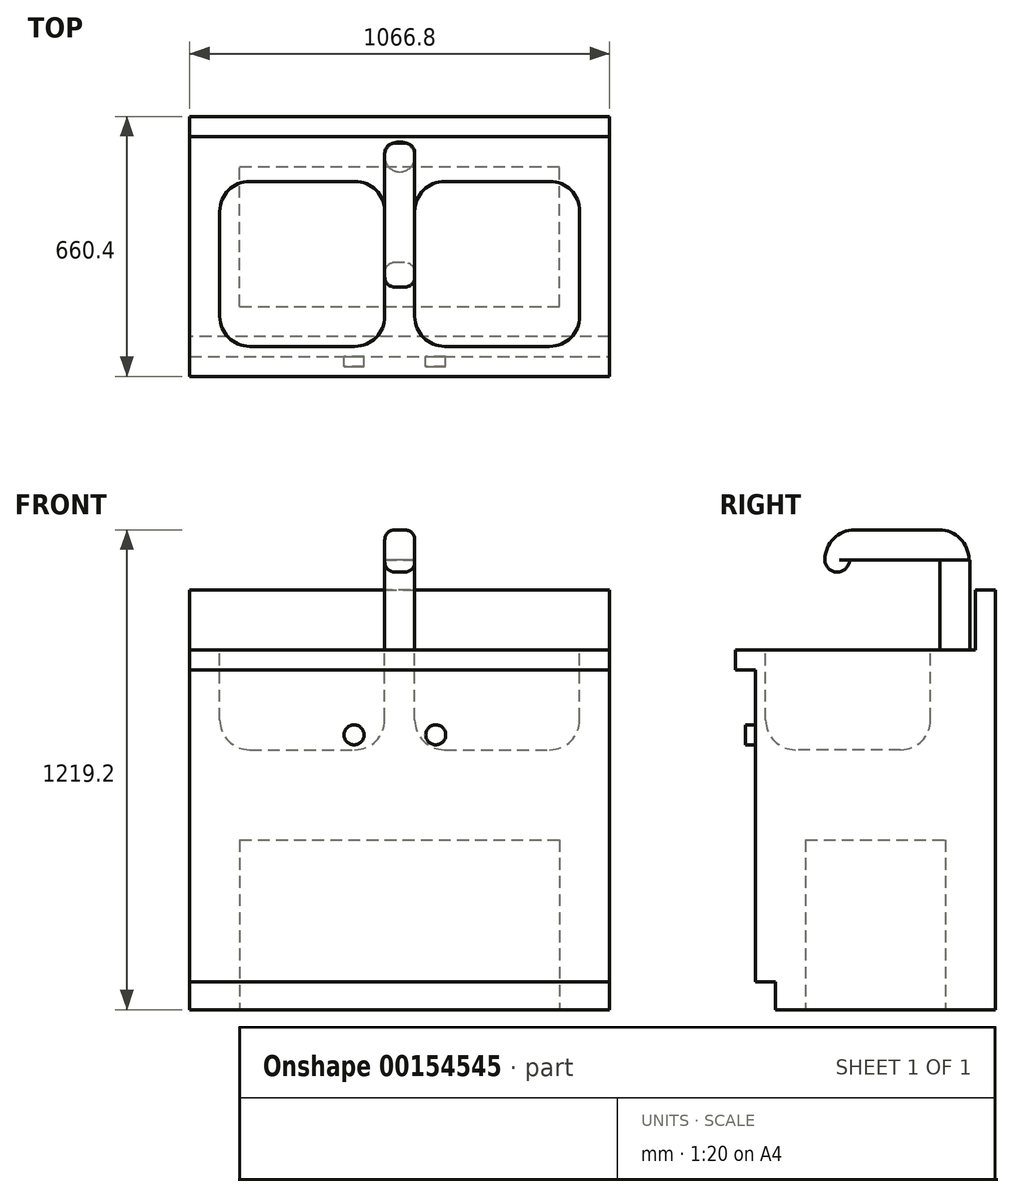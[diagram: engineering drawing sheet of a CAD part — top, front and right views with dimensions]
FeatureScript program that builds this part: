
annotation { "Feature Type Name" : "Feature", "Feature Type Description" : "" }
export const myFeature = defineFeature(function(context is Context, id is Id, definition is map)
    precondition{}
    {
        {
            var Q0;
            Q0=qCreatedBy(makeId("Top.planeOp"),FACE);
            var sketch = newSketch(context, id + "F0", { "sketchPlane" : qUnion([Q0])});
            skLineSegment(sketch, "E0.bottom", {"start": v(533.4, 304.8) * mm, "end": v(-533.4, 304.8) * mm});
            skLineSegment(sketch, "E0.top", {"start": v(533.4, -304.8) * mm, "end": v(-533.4, -304.8) * mm});
            skLineSegment(sketch, "E0.left", {"start": v(533.4, 304.8) * mm, "end": v(533.4, -304.8) * mm});
            skLineSegment(sketch, "E0.right", {"start": v(-533.4, 304.8) * mm, "end": v(-533.4, -304.8) * mm});
            skPoint(sketch, "E0.middle", {"position": v(0, 0) * mm});
            skSolve(sketch);
        }
        {
            var Q0;
            Q0=makeQuery(id+"F0.imprint","IMPRINT",FACE,{"disambiguationData":[TD([[makeQuery(id+"F0.imprint","IMPRINT",EDGE,{"derivedFrom":sQuery(id+"F0.wireOp",EDGE,"E0.bottom")}),1.0]])]});
            extrude(context, id + "F1", {"entities" : qUnion([Q0]), "depth" : 914.4 * mm});
        }
        {
            var Q0;
            Q0=makeQuery(id+"F1.opExtrude","CAP_FACE",FACE,{"disambiguationData":[OSD([sQuery(id+"F0.wireOp",EDGE,"E0.bottom"),sQuery(id+"F0.wireOp",EDGE,"E0.top"),sQuery(id+"F0.wireOp",EDGE,"E0.left"),sQuery(id+"F0.wireOp",EDGE,"E0.right")])],"isStart":false});
            var sketch = newSketch(context, id + "F2", { "sketchPlane" : qUnion([Q0])});
            skLineSegment(sketch, "E1.bottom", {"start": v(-533.4, 304.8) * mm, "end": v(533.4, 304.8) * mm});
            skLineSegment(sketch, "E1.top", {"start": v(-533.4, -355.6) * mm, "end": v(533.4, -355.6) * mm});
            skLineSegment(sketch, "E1.left", {"start": v(-533.4, 304.8) * mm, "end": v(-533.4, -355.6) * mm});
            skLineSegment(sketch, "E1.right", {"start": v(533.4, 304.8) * mm, "end": v(533.4, -355.6) * mm});
            skSolve(sketch);
        }
        {
            var Q0;
            {var subQ0=sQuery(id+"F2.wireOp",EDGE,"E1.top");Q0=makeQuery(id+"F2.imprint","IMPRINT",FACE,{"disambiguationData":[TD([[makeQuery(id+"F2.imprint","IMPRINT",EDGE,{"derivedFrom":subQ0}),1.0]])]});}
            var Q1;
            {var subQ0=sQuery(id+"F2.wireOp",EDGE,"E1.bottom");Q1=makeQuery(id+"F2.imprint","IMPRINT",FACE,{"disambiguationData":[TD([[makeQuery(id+"F2.imprint","IMPRINT",EDGE,{"derivedFrom":subQ0}),1.0]])]});}
            extrude(context, id + "F3", {"entities" : qUnion([Q0, Q1]), "operationType" : NewBodyOperationType.ADD, "oppositeDirection" : true, "depth" : 50.8 * mm});
        }
        {
            var Q0;
            Q0=makeQuery(id+"F3.boolean.opBoolean","MERGE",FACE,{"derivedFrom":[makeQuery(id+"F1.opExtrude","CAP_FACE",FACE,{"disambiguationData":[OSD([sQuery(id+"F0.wireOp",EDGE,"E0.bottom"),sQuery(id+"F0.wireOp",EDGE,"E0.top"),sQuery(id+"F0.wireOp",EDGE,"E0.left"),sQuery(id+"F0.wireOp",EDGE,"E0.right")])],"isStart":false}),makeQuery(id+"F3.opExtrude","CAP_FACE",FACE,{"disambiguationData":[OSD([sQuery(id+"F2.wireOp",EDGE,"E1.bottom"),sQuery(id+"F2.wireOp",EDGE,"E1.top"),sQuery(id+"F2.wireOp",EDGE,"E1.left"),sQuery(id+"F2.wireOp",EDGE,"E1.right")])],"isStart":true})]});
            var sketch = newSketch(context, id + "F4", { "sketchPlane" : qUnion([Q0])});
            skLineSegment(sketch, "E2.bottom", {"start": v(-533.4, 304.8) * mm, "end": v(533.4, 304.8) * mm});
            skLineSegment(sketch, "E2.top", {"start": v(-533.4, 254) * mm, "end": v(533.4, 254) * mm});
            skLineSegment(sketch, "E2.left", {"start": v(-533.4, 304.8) * mm, "end": v(-533.4, 254) * mm});
            skLineSegment(sketch, "E2.right", {"start": v(533.4, 304.8) * mm, "end": v(533.4, 254) * mm});
            skLineSegment(sketch, "E3.bottom", {"start": v(-457.2, 139.7) * mm, "end": v(-38.1, 139.7) * mm});
            skLineSegment(sketch, "E3.top", {"start": v(-457.2, -279.4) * mm, "end": v(-38.1, -279.4) * mm});
            skLineSegment(sketch, "E3.left", {"start": v(-457.2, 139.7) * mm, "end": v(-457.2, -279.4) * mm});
            skLineSegment(sketch, "E3.right", {"start": v(-38.1, 139.7) * mm, "end": v(-38.1, -279.4) * mm});
            skLineSegment(sketch, "E4.bottom", {"start": v(38.1, 139.7) * mm, "end": v(457.2, 139.7) * mm});
            skLineSegment(sketch, "E4.top", {"start": v(38.1, -279.4) * mm, "end": v(457.2, -279.4) * mm});
            skLineSegment(sketch, "E4.left", {"start": v(38.1, 139.7) * mm, "end": v(38.1, -279.4) * mm});
            skLineSegment(sketch, "E4.right", {"start": v(457.2, 139.7) * mm, "end": v(457.2, -279.4) * mm});
            skCircle(sketch, "E5", {"center": v(0, 201.8) * mm, "radius": 38.1 * mm});
            skSolve(sketch);
        }
        {
            var Q0;
            Q0=makeQuery(id+"F4.imprint","IMPRINT",FACE,{"disambiguationData":[TD([[makeQuery(id+"F4.imprint","IMPRINT",EDGE,{"derivedFrom":sQuery(id+"F4.wireOp",EDGE,"E2.bottom")}),1.0]])]});
            extrude(context, id + "F5", {"entities" : qUnion([Q0]), "operationType" : NewBodyOperationType.ADD, "depth" : 152.4 * mm});
        }
        {
            var Q0;
            Q0=makeQuery(id+"F4.imprint","IMPRINT",FACE,{"disambiguationData":[TD([[makeQuery(id+"F4.imprint","IMPRINT",EDGE,{"derivedFrom":sQuery(id+"F4.wireOp",EDGE,"E3.bottom")}),-1.0]])]});
            var Q1;
            Q1=makeQuery(id+"F4.imprint","IMPRINT",FACE,{"disambiguationData":[TD([[makeQuery(id+"F4.imprint","IMPRINT",EDGE,{"derivedFrom":sQuery(id+"F4.wireOp",EDGE,"E4.bottom")}),-1.0]])]});
            extrude(context, id + "F6", {"entities" : qUnion([Q0, Q1]), "operationType" : NewBodyOperationType.REMOVE, "oppositeDirection" : true, "depth" : 254 * mm});
        }
        {
            var Q0;
            Q0=makeQuery(id+"F6.boolean.opBoolean","COPY",FACE,{"derivedFrom":makeQuery(id+"F6.opExtrude","CAP_FACE",FACE,{"disambiguationData":[OSD([sQuery(id+"F4.wireOp",EDGE,"E3.bottom"),sQuery(id+"F4.wireOp",EDGE,"E3.top"),sQuery(id+"F4.wireOp",EDGE,"E3.left"),sQuery(id+"F4.wireOp",EDGE,"E3.right")])],"isStart":false})});
            var Q1;
            Q1=makeQuery(id+"F6.boolean.opBoolean","COPY",FACE,{"derivedFrom":makeQuery(id+"F6.opExtrude","CAP_FACE",FACE,{"disambiguationData":[OSD([sQuery(id+"F4.wireOp",EDGE,"E4.bottom"),sQuery(id+"F4.wireOp",EDGE,"E4.top"),sQuery(id+"F4.wireOp",EDGE,"E4.left"),sQuery(id+"F4.wireOp",EDGE,"E4.right")])],"isStart":false})});
            var Q2;
            Q2=makeQuery(id+"F6.boolean.opBoolean","COPY",EDGE,{"derivedFrom":makeQuery(id+"F6.opExtrude","SWEPT_EDGE",EDGE,{"disambiguationData":[OSD([sQuery(id+"F4.wireOp",EDGE,"E4.bottom"),sQuery(id+"F4.wireOp",EDGE,"E4.right")])]})});
            var Q3;
            Q3=makeQuery(id+"F6.boolean.opBoolean","COPY",EDGE,{"derivedFrom":makeQuery(id+"F6.opExtrude","SWEPT_EDGE",EDGE,{"disambiguationData":[OSD([sQuery(id+"F4.wireOp",EDGE,"E4.bottom"),sQuery(id+"F4.wireOp",EDGE,"E4.left")])]})});
            var Q4;
            Q4=makeQuery(id+"F6.boolean.opBoolean","COPY",EDGE,{"derivedFrom":makeQuery(id+"F6.opExtrude","SWEPT_EDGE",EDGE,{"disambiguationData":[OSD([sQuery(id+"F4.wireOp",EDGE,"E4.top"),sQuery(id+"F4.wireOp",EDGE,"E4.right")])]})});
            var Q5;
            Q5=makeQuery(id+"F6.boolean.opBoolean","COPY",EDGE,{"derivedFrom":makeQuery(id+"F6.opExtrude","SWEPT_EDGE",EDGE,{"disambiguationData":[OSD([sQuery(id+"F4.wireOp",EDGE,"E4.top"),sQuery(id+"F4.wireOp",EDGE,"E4.left")])]})});
            var Q6;
            Q6=makeQuery(id+"F6.boolean.opBoolean","COPY",EDGE,{"derivedFrom":makeQuery(id+"F6.opExtrude","SWEPT_EDGE",EDGE,{"disambiguationData":[OSD([sQuery(id+"F4.wireOp",EDGE,"E3.top"),sQuery(id+"F4.wireOp",EDGE,"E3.left")])]})});
            var Q7;
            Q7=makeQuery(id+"F6.boolean.opBoolean","COPY",EDGE,{"derivedFrom":makeQuery(id+"F6.opExtrude","SWEPT_EDGE",EDGE,{"disambiguationData":[OSD([sQuery(id+"F4.wireOp",EDGE,"E3.top"),sQuery(id+"F4.wireOp",EDGE,"E3.right")])]})});
            var Q8;
            Q8=makeQuery(id+"F6.boolean.opBoolean","COPY",EDGE,{"derivedFrom":makeQuery(id+"F6.opExtrude","SWEPT_EDGE",EDGE,{"disambiguationData":[OSD([sQuery(id+"F4.wireOp",EDGE,"E3.bottom"),sQuery(id+"F4.wireOp",EDGE,"E3.right")])]})});
            var Q9;
            Q9=makeQuery(id+"F6.boolean.opBoolean","COPY",EDGE,{"derivedFrom":makeQuery(id+"F6.opExtrude","SWEPT_EDGE",EDGE,{"disambiguationData":[OSD([sQuery(id+"F4.wireOp",EDGE,"E3.bottom"),sQuery(id+"F4.wireOp",EDGE,"E3.left")])]})});
            fillet(context, id + "F7", {"entities" : qUnion([Q0, Q1, Q2, Q3, Q4, Q5, Q6, Q7, Q8, Q9]), "radius" : 76.2 * mm, "tangentPropagation" : true, "allowEdgeOverflow" : false});
        }
        {
            var Q0;
            Q0=makeQuery(id+"F4.imprint","IMPRINT",FACE,{"disambiguationData":[TD([[makeQuery(id+"F4.imprint","IMPRINT",EDGE,{"derivedFrom":sQuery(id+"F4.wireOp",EDGE,"E5")}),1.0]])]});
            extrude(context, id + "F8", {"entities" : qUnion([Q0]), "operationType" : NewBodyOperationType.ADD, "depth" : 228.6 * mm});
        }
        {
            var Q0;
            Q0=qCreatedBy(makeId("Right.planeOp"),FACE);
            var sketch = newSketch(context, id + "F9", { "sketchPlane" : qUnion([Q0])});
            skLineSegment(sketch, "E6.bottom", {"start": v(-52.72, 1219.2) * mm, "end": v(160.83, 1219.2) * mm});
            skLineSegment(sketch, "E6.top", {"start": v(-128.92, 1143) * mm, "end": v(237.03, 1143) * mm});
            skLineSegment(sketch, "E6.left", {"start": v(-128.92, 1143) * mm, "end": v(-128.92, 1143) * mm});
            skLineSegment(sketch, "E6.right", {"start": v(237.03, 1143) * mm, "end": v(237.03, 1143) * mm});
            skPoint(sketch, "E7.visualSharp", {"position": v(237.03, 1219.2) * mm});
            skArc(sketch, "E7.filletArc", {"start": v(237.03, 1143) * mm, "mid": v(214.71, 1196.88) * mm, "end": v(160.83, 1219.2) * mm});
            skCircle(sketch, "E8", {"center": v(-97.76, 1143) * mm, "radius": 31.16 * mm});
            skPoint(sketch, "E9.visualSharp", {"position": v(-128.92, 1219.2) * mm});
            skArc(sketch, "E9.filletArc", {"start": v(-52.72, 1219.2) * mm, "mid": v(-106.6, 1196.88) * mm, "end": v(-128.92, 1143) * mm});
            skSolve(sketch);
        }
        {
            var Q0;
            Q0=makeQuery(id+"F9.imprint","IMPRINT",FACE,{"disambiguationData":[TD([[makeQuery(id+"F9.imprint","IMPRINT",EDGE,{"derivedFrom":sQuery(id+"F9.wireOp",EDGE,"E6.bottom")}),-1.0]])]});
            var Q1;
            {var subQ0=sQuery(id+"F9.wireOp",EDGE,"E8");var subQ1=sQuery(id+"F9.wireOp",EDGE,"E6.top");var subQ3=makeQuery(id+"F9.imprint","INTERSECT",VERTEX,{"derivedFrom":[subQ1,subQ0]});Q1=makeQuery(id+"F9.imprint","IMPRINT",FACE,{"disambiguationData":[TD([[makeQuery(id+"F9.imprint","IMPRINT",EDGE,{"disambiguationData":[TD([[subQ3,1.0]])],"derivedFrom":subQ1}),1.0]])]});}
            var Q2;
            {var subQ0=sQuery(id+"F9.wireOp",EDGE,"E8");var subQ1=sQuery(id+"F9.wireOp",EDGE,"E6.top");var subQ3=makeQuery(id+"F9.imprint","INTERSECT",VERTEX,{"derivedFrom":[subQ1,subQ0]});Q2=makeQuery(id+"F9.imprint","IMPRINT",FACE,{"disambiguationData":[TD([[makeQuery(id+"F9.imprint","IMPRINT",EDGE,{"disambiguationData":[TD([[subQ3,1.0]])],"derivedFrom":subQ1}),-1.0]])]});}
            extrude(context, id + "F10", {"entities" : qUnion([Q0, Q1, Q2]), "operationType" : NewBodyOperationType.ADD, "depth" : 76.2 * mm, "symmetric" : true});
        }
        {
            var Q0;
            Q0=makeQuery(id+"F10.opExtrude","CAP_EDGE",EDGE,{"disambiguationData":[OSD([sQuery(id+"F9.wireOp",EDGE,"E6.bottom")])],"isStart":false});
            var Q1;
            Q1=makeQuery(id+"F10.opExtrude","CAP_EDGE",EDGE,{"disambiguationData":[OSD([sQuery(id+"F9.wireOp",EDGE,"E6.bottom")])],"isStart":true});
            fillet(context, id + "F11", {"entities" : qUnion([Q0, Q1]), "radius" : 25.4 * mm, "tangentPropagation" : true, "allowEdgeOverflow" : false});
        }
        {
            var Q0;
            Q0=makeQuery(id+"F1.opExtrude","CAP_FACE",FACE,{"disambiguationData":[OSD([sQuery(id+"F0.wireOp",EDGE,"E0.bottom"),sQuery(id+"F0.wireOp",EDGE,"E0.top"),sQuery(id+"F0.wireOp",EDGE,"E0.left"),sQuery(id+"F0.wireOp",EDGE,"E0.right")])],"isStart":true});
            var sketch = newSketch(context, id + "F12", { "sketchPlane" : qUnion([Q0])});
            skLineSegment(sketch, "E10.bottom", {"start": v(-406.4, 177.8) * mm, "end": v(406.4, 177.8) * mm});
            skLineSegment(sketch, "E10.top", {"start": v(-406.4, -177.8) * mm, "end": v(406.4, -177.8) * mm});
            skLineSegment(sketch, "E10.left", {"start": v(-406.4, 177.8) * mm, "end": v(-406.4, -177.8) * mm});
            skLineSegment(sketch, "E10.right", {"start": v(406.4, 177.8) * mm, "end": v(406.4, -177.8) * mm});
            skSolve(sketch);
        }
        {
            var Q0;
            Q0=makeQuery(id+"F12.imprint","IMPRINT",FACE,{"disambiguationData":[TD([[makeQuery(id+"F12.imprint","IMPRINT",EDGE,{"derivedFrom":sQuery(id+"F12.wireOp",EDGE,"E10.bottom")}),-1.0]])]});
            extrude(context, id + "F13", {"entities" : qUnion([Q0]), "operationType" : NewBodyOperationType.REMOVE, "oppositeDirection" : true, "depth" : 431.3 * mm});
        }
        {
            var Q0;
            Q0=makeQuery(id+"F1.opExtrude","SWEPT_FACE",FACE,{"disambiguationData":[OSD([sQuery(id+"F0.wireOp",EDGE,"E0.top")])]});
            var sketch = newSketch(context, id + "F14", { "sketchPlane" : qUnion([Q0])});
            skLineSegment(sketch, "E11.bottom", {"start": v(-533.4, 0) * mm, "end": v(533.4, 0) * mm});
            skLineSegment(sketch, "E11.top", {"start": v(-533.4, 71.15) * mm, "end": v(533.4, 71.15) * mm});
            skLineSegment(sketch, "E11.left", {"start": v(-533.4, 0) * mm, "end": v(-533.4, 71.15) * mm});
            skLineSegment(sketch, "E11.right", {"start": v(533.4, 0) * mm, "end": v(533.4, 71.15) * mm});
            skSolve(sketch);
        }
        {
            var Q0;
            Q0=makeQuery(id+"F14.imprint","IMPRINT",FACE,{"disambiguationData":[TD([[makeQuery(id+"F14.imprint","IMPRINT",EDGE,{"derivedFrom":sQuery(id+"F14.wireOp",EDGE,"E11.bottom")}),-1.0]])]});
            extrude(context, id + "F15", {"entities" : qUnion([Q0]), "operationType" : NewBodyOperationType.REMOVE, "oppositeDirection" : true, "depth" : 50.8 * mm});
        }
        {
            var Q0;
            Q0=makeQuery(id+"F1.opExtrude","SWEPT_FACE",FACE,{"disambiguationData":[OSD([sQuery(id+"F0.wireOp",EDGE,"E0.top")])]});
            var sketch = newSketch(context, id + "F16", { "sketchPlane" : qUnion([Q0])});
            skCircle(sketch, "E12", {"center": v(-116.1, 698.15) * mm, "radius": 25.4 * mm});
            skCircle(sketch, "E13", {"center": v(91.39, 698.15) * mm, "radius": 25.4 * mm});
            skLineSegment(sketch, "E14", {"start": v(-533.4, 698.15) * mm, "end": v(-116.1, 698.15) * mm, "construction": true});
            skLineSegment(sketch, "E15", {"start": v(91.39, 698.15) * mm, "end": v(533.4, 698.15) * mm, "construction": true});
            skLineSegment(sketch, "E16", {"start": v(-116.1, 698.15) * mm, "end": v(91.39, 698.15) * mm, "construction": true});
            skLineSegment(sketch, "E17", {"start": v(0, 71.15) * mm, "end": v(-12.35, 698.15) * mm, "construction": true});
            skSolve(sketch);
        }
        {
            var Q0;
            Q0=makeQuery(id+"F16.imprint","IMPRINT",FACE,{"disambiguationData":[TD([[makeQuery(id+"F16.imprint","IMPRINT",EDGE,{"derivedFrom":sQuery(id+"F16.wireOp",EDGE,"E12")}),1.0]])]});
            var Q1;
            Q1=makeQuery(id+"F16.imprint","IMPRINT",FACE,{"disambiguationData":[TD([[makeQuery(id+"F16.imprint","IMPRINT",EDGE,{"derivedFrom":sQuery(id+"F16.wireOp",EDGE,"E13")}),1.0]])]});
            extrude(context, id + "F17", {"entities" : qUnion([Q0, Q1]), "operationType" : NewBodyOperationType.ADD, "depth" : 25.4 * mm});
        }
    });
